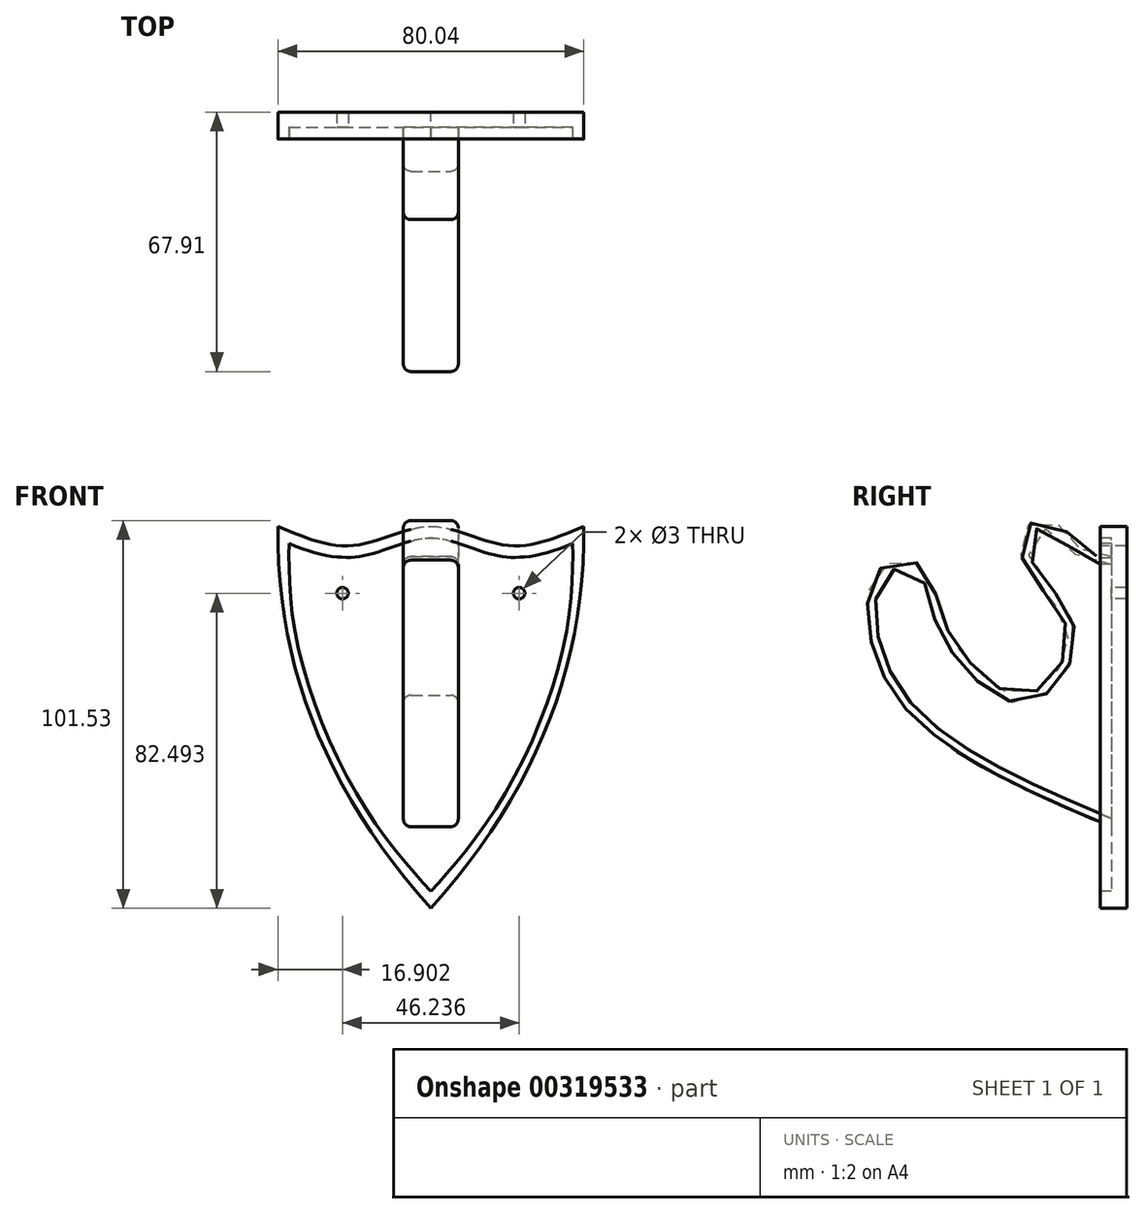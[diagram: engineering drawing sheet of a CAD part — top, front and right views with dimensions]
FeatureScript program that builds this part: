
annotation { "Feature Type Name" : "Feature", "Feature Type Description" : "" }
export const myFeature = defineFeature(function(context is Context, id is Id, definition is map)
    precondition{}
    {
        {
            var Q0;
            Q0=qCreatedBy(makeId("Front.planeOp"),FACE);
            var sketch = newSketch(context, id + "F0", { "sketchPlane" : qUnion([Q0])});
            skPoint(sketch, "E0.middle", {"position": v(0, 0) * mm});
            skLineSegment(sketch, "E1", {"start": v(0, -50) * mm, "end": v(0, 50) * mm, "construction": true});
            skLineSegment(sketch, "E2", {"start": v(-40, 50) * mm, "end": v(40, 50) * mm, "construction": true});
            skLineSegment(sketch, "E3", {"start": v(-40, 50) * mm, "end": v(-20, 50) * mm, "construction": true});
            skLineSegment(sketch, "E4.MirrorCS", {"start": v(40, 50) * mm, "end": v(20, 50) * mm, "construction": true});
            skLineSegment(sketch, "E5", {"start": v(-20, 50) * mm, "end": v(-20, 45) * mm, "construction": true});
            skLineSegment(sketch, "E6.MirrorCS", {"start": v(20, 50) * mm, "end": v(20, 45) * mm, "construction": true});
            skFitSpline(sketch, "E7", {"points": [v(-40, 50) * mm, v(-20, 45) * mm, v(0, 50) * mm, v(20, 45) * mm, v(40, 50) * mm], "startDerivative": vector(80, -34.29) * mm, "endDerivative": vector(80, 34.29) * mm});
            skFitSpline(sketch, "E8", {"points": [v(-40, 50) * mm, v(0, -50) * mm], "startDerivative": vector(-2, -110.25) * mm, "endDerivative": vector(80.35, -89.05) * mm});
            skFitSpline(sketch, "E9.MirrorCS", {"points": [v(40, 50) * mm, v(0, -50) * mm], "startDerivative": vector(2, -110.25) * mm, "endDerivative": vector(-80.35, -89.05) * mm});
            skSolve(sketch);
        }
        {
            var Q0;
            Q0 = qSketchRegion(id + "F0", true);
            extrude(context, id + "F1", {"entities" : qUnion([Q0]), "depth" : 7 * mm});
        }
        {
            var Q0;
            Q0=makeQuery(id+"F1.opExtrude","CAP_FACE",FACE,{"disambiguationData":[OSD([sQuery(id+"F0.wireOp",EDGE,"E7"),sQuery(id+"F0.wireOp",EDGE,"E8"),sQuery(id+"F0.wireOp",EDGE,"E9.MirrorCS")])],"isStart":false});
            var sketch = newSketch(context, id + "F2", { "sketchPlane" : qUnion([Q0])});
            skFitSpline(sketch, "E10.0", {"points": [v(-41.18, 47.24) * mm, v(-39.52, 46.53) * mm, v(-36.98, 45.44) * mm, v(-33.5, 44.13) * mm, v(-30.86, 43.26) * mm, v(-28.15, 42.55) * mm, v(-25.85, 42.14) * mm, v(-23.98, 41.95) * mm, v(-22.56, 41.88) * mm, v(-21.13, 41.9) * mm, v(-19.68, 42) * mm, v(-18.24, 42.2) * mm, v(-16.84, 42.48) * mm, v(-15.47, 42.82) * mm, v(-13.68, 43.33) * mm, v(-11.51, 44.05) * mm, v(-9, 44.95) * mm, v(-6.58, 45.77) * mm, v(-4.65, 46.33) * mm, v(-3.16, 46.67) * mm, v(-2.07, 46.86) * mm, v(-1.2, 46.95) * mm, v(-0.5, 47) * mm, v(0, 47) * mm, v(0.5, 47) * mm, v(1.2, 46.95) * mm, v(2.07, 46.86) * mm, v(3.16, 46.67) * mm, v(4.65, 46.33) * mm, v(6.58, 45.77) * mm, v(9, 44.95) * mm, v(11.51, 44.05) * mm, v(13.68, 43.33) * mm, v(15.47, 42.82) * mm, v(16.84, 42.48) * mm, v(18.24, 42.2) * mm, v(19.68, 42) * mm, v(21.13, 41.9) * mm, v(22.56, 41.88) * mm, v(23.98, 41.95) * mm, v(25.85, 42.14) * mm, v(28.15, 42.55) * mm, v(30.86, 43.26) * mm, v(33.5, 44.13) * mm, v(36.98, 45.44) * mm, v(39.52, 46.53) * mm, v(41.18, 47.24) * mm]});
            skFitSpline(sketch, "E10.1", {"points": [v(-37, 49.95) * mm, v(-37.16, 40.96) * mm, v(-35.7, 23.39) * mm, v(-28.35, -1.73) * mm, v(-15.94, -25.61) * mm, v(-4.37, -40.68) * mm, v(2.23, -48) * mm]});
            skFitSpline(sketch, "E10.2", {"points": [v(37, 49.95) * mm, v(37.16, 40.96) * mm, v(35.7, 23.39) * mm, v(28.35, -1.73) * mm, v(15.94, -25.61) * mm, v(4.37, -40.68) * mm, v(-2.23, -48) * mm]});
            skSolve(sketch);
        }
        {
            var Q0;
            Q0 = qSketchRegion(id + "F2", true);
            extrude(context, id + "F3", {"entities" : qUnion([Q0]), "operationType" : NewBodyOperationType.REMOVE, "oppositeDirection" : true, "depth" : 3 * mm});
        }
        {
            var Q0;
            Q0=qCreatedBy(makeId("Right.planeOp"),FACE);
            var sketch = newSketch(context, id + "F4", { "sketchPlane" : qUnion([Q0])});
            skFitSpline(sketch, "E11.0", {"points": [v(-4, 49.95) * mm, v(-4, 40.96) * mm, v(-4, 23.39) * mm, v(-4, -1.73) * mm, v(-4, -25.61) * mm, v(-4, -40.68) * mm, v(-4, -48) * mm]});
            skFitSpline(sketch, "E12", {"points": [v(-4, -28.67) * mm, v(-27.76, -18.15) * mm, v(-60.42, 5.44) * mm, v(-67.68, 31.94) * mm, v(-62.6, 40.28) * mm, v(-53.53, 39.56) * mm, v(-49.17, 28.67) * mm, v(-41.92, 15.24) * mm, v(-28.13, 5.8) * mm, v(-18.33, 11.98) * mm, v(-15.79, 23.59) * mm, v(-22.32, 33.75) * mm, v(-28.13, 44.64) * mm, v(-24.5, 51.17) * mm, v(-16.15, 49) * mm, v(-11.07, 43.19) * mm, v(-4, 42.1) * mm], "startDerivative": vector(-256.56, 106.7) * mm, "endDerivative": vector(174.24, 4.29) * mm});
            skSolve(sketch);
        }
        {
            var Q0;
            {var subQ0=sQuery(id+"F4.wireOp",EDGE,"E12");Q0=makeQuery(id+"F4.imprint","IMPRINT",FACE,{"disambiguationData":[TD([[makeQuery(id+"F4.imprint","IMPRINT",EDGE,{"derivedFrom":subQ0}),-1.0]])]});}
            extrude(context, id + "F5", {"entities" : qUnion([Q0]), "operationType" : NewBodyOperationType.ADD, "depth" : 14.4 * mm, "symmetric" : true});
        }
        {
            var Q0;
            Q0=makeQuery(id+"F2.imprint","IMPRINT",FACE,{"disambiguationData":[TD([[makeQuery(id+"F2.imprint","IMPRINT",EDGE,{"derivedFrom":sQuery(id+"F2.wireOp",EDGE,"E10.0")}),-1.0]])]});
            var sketch = newSketch(context, id + "F6", { "sketchPlane" : qUnion([Q0])});
            skCircle(sketch, "E13", {"center": v(-23.12, 32.5) * mm, "radius": 1.5 * mm});
            skCircle(sketch, "E14.MirrorC", {"center": v(23.12, 32.5) * mm, "radius": 1.5 * mm});
            skSolve(sketch);
        }
        {
            var Q0;
            Q0 = qSketchRegion(id + "F6", true);
            extrude(context, id + "F7", {"entities" : qUnion([Q0]), "operationType" : NewBodyOperationType.REMOVE, "endBound" : BoundingType.THROUGH_ALL, "oppositeDirection" : true, "depth" : 25 * mm});
        }
        {
            var Q0;
            Q0=makeQuery(id+"F5.opExtrude","CAP_EDGE",EDGE,{"disambiguationData":[OSD([sQuery(id+"F4.wireOp",EDGE,"E12")])],"isStart":false});
            var Q1;
            Q1=makeQuery(id+"F5.opExtrude","CAP_EDGE",EDGE,{"disambiguationData":[OSD([sQuery(id+"F4.wireOp",EDGE,"E12")])],"isStart":true});
            fillet(context, id + "F8", {"entities" : qUnion([Q0, Q1]), "radius" : 2 * mm, "tangentPropagation" : true, "allowEdgeOverflow" : false});
        }
    });
